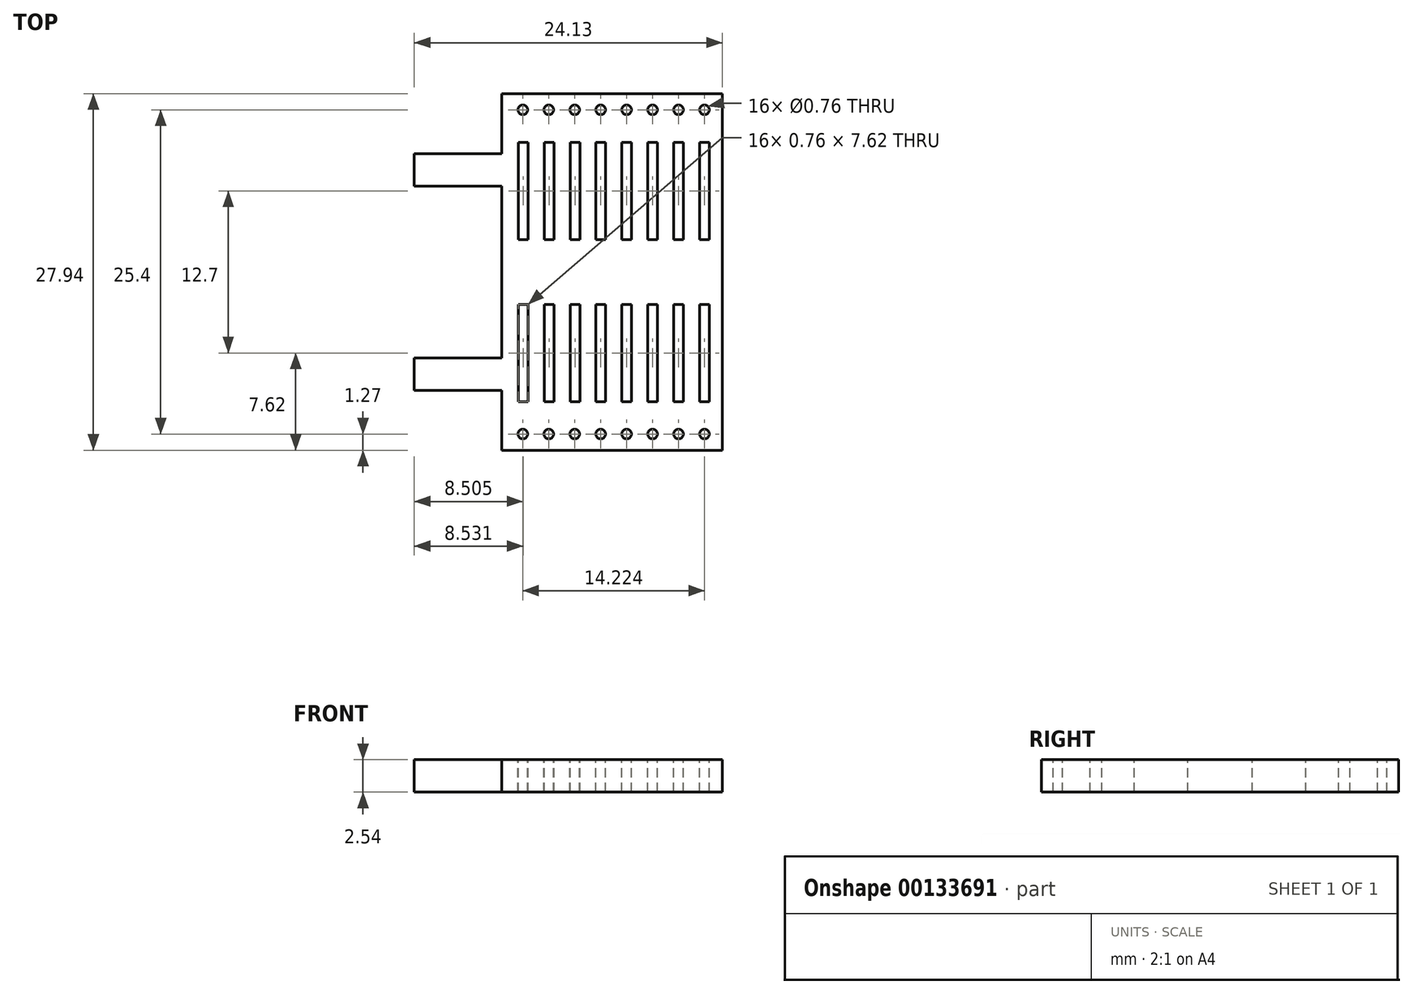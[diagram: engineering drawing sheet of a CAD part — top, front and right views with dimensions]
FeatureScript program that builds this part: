
annotation { "Feature Type Name" : "Feature", "Feature Type Description" : "" }
export const myFeature = defineFeature(function(context is Context, id is Id, definition is map)
    precondition{}
    {
        {
            var Q0;
            Q0=qCreatedBy(makeId("Top.planeOp"),FACE);
            var sketch = newSketch(context, id + "F0", { "sketchPlane" : qUnion([Q0])});
            skLineSegment(sketch, "E0.bottom", {"start": v(8.64, 13.97) * mm, "end": v(-8.64, 13.97) * mm});
            skLineSegment(sketch, "E0.top", {"start": v(8.64, -13.97) * mm, "end": v(-8.64, -13.97) * mm});
            skLineSegment(sketch, "E0.left", {"start": v(8.64, 13.97) * mm, "end": v(8.64, -13.97) * mm});
            skLineSegment(sketch, "E0.right", {"start": v(-8.64, 13.97) * mm, "end": v(-8.64, -13.97) * mm});
            skPoint(sketch, "E0.middle", {"position": v(0, 0) * mm});
            skLineSegment(sketch, "E1.bottom", {"start": v(6.86, 10.16) * mm, "end": v(7.62, 10.16) * mm});
            skLineSegment(sketch, "E1.top", {"start": v(6.86, 2.54) * mm, "end": v(7.62, 2.54) * mm});
            skLineSegment(sketch, "E1.left", {"start": v(6.86, 10.16) * mm, "end": v(6.86, 2.54) * mm});
            skLineSegment(sketch, "E1.right", {"start": v(7.62, 10.16) * mm, "end": v(7.62, 2.54) * mm});
            skCircle(sketch, "E2", {"center": v(7.24, 12.7) * mm, "radius": 0.38 * mm});
            skLineSegment(sketch, "E3.1.0.0", {"start": v(5.6, 10.16) * mm, "end": v(5.6, 2.54) * mm});
            skLineSegment(sketch, "E3.1.0.1", {"start": v(4.83, 10.16) * mm, "end": v(4.83, 2.54) * mm});
            skLineSegment(sketch, "E3.1.0.2", {"start": v(4.83, 10.16) * mm, "end": v(5.6, 10.16) * mm});
            skLineSegment(sketch, "E3.1.0.3", {"start": v(4.83, 2.54) * mm, "end": v(5.6, 2.54) * mm});
            skLineSegment(sketch, "E3.2.0.0", {"start": v(3.56, 10.16) * mm, "end": v(3.56, 2.54) * mm});
            skLineSegment(sketch, "E3.2.0.1", {"start": v(2.8, 10.16) * mm, "end": v(2.8, 2.54) * mm});
            skLineSegment(sketch, "E3.2.0.2", {"start": v(2.8, 10.16) * mm, "end": v(3.56, 10.16) * mm});
            skLineSegment(sketch, "E3.2.0.3", {"start": v(2.8, 2.54) * mm, "end": v(3.56, 2.54) * mm});
            skLineSegment(sketch, "E3.3.0.0", {"start": v(1.54, 10.16) * mm, "end": v(1.54, 2.54) * mm});
            skLineSegment(sketch, "E3.3.0.1", {"start": v(0.77, 10.16) * mm, "end": v(0.77, 2.54) * mm});
            skLineSegment(sketch, "E3.3.0.2", {"start": v(0.77, 10.16) * mm, "end": v(1.54, 10.16) * mm});
            skLineSegment(sketch, "E3.3.0.3", {"start": v(0.77, 2.54) * mm, "end": v(1.54, 2.54) * mm});
            skLineSegment(sketch, "E3.4.0.0", {"start": v(-0.5, 10.16) * mm, "end": v(-0.5, 2.54) * mm});
            skLineSegment(sketch, "E3.4.0.1", {"start": v(-1.26, 10.16) * mm, "end": v(-1.26, 2.54) * mm});
            skLineSegment(sketch, "E3.4.0.2", {"start": v(-1.26, 10.16) * mm, "end": v(-0.5, 10.16) * mm});
            skLineSegment(sketch, "E3.4.0.3", {"start": v(-1.26, 2.54) * mm, "end": v(-0.5, 2.54) * mm});
            skLineSegment(sketch, "E3.5.0.0", {"start": v(-2.52, 10.16) * mm, "end": v(-2.52, 2.54) * mm});
            skLineSegment(sketch, "E3.5.0.1", {"start": v(-3.28, 10.16) * mm, "end": v(-3.28, 2.54) * mm});
            skLineSegment(sketch, "E3.5.0.2", {"start": v(-3.28, 10.16) * mm, "end": v(-2.52, 10.16) * mm});
            skLineSegment(sketch, "E3.5.0.3", {"start": v(-3.28, 2.54) * mm, "end": v(-2.52, 2.54) * mm});
            skLineSegment(sketch, "E3.6.0.0", {"start": v(-4.55, 10.16) * mm, "end": v(-4.55, 2.54) * mm});
            skLineSegment(sketch, "E3.6.0.1", {"start": v(-5.31, 10.16) * mm, "end": v(-5.31, 2.54) * mm});
            skLineSegment(sketch, "E3.6.0.2", {"start": v(-5.31, 10.16) * mm, "end": v(-4.55, 10.16) * mm});
            skLineSegment(sketch, "E3.6.0.3", {"start": v(-5.31, 2.54) * mm, "end": v(-4.55, 2.54) * mm});
            skLineSegment(sketch, "E3.7.0.0", {"start": v(-6.58, 10.16) * mm, "end": v(-6.58, 2.54) * mm});
            skLineSegment(sketch, "E3.7.0.1", {"start": v(-7.34, 10.16) * mm, "end": v(-7.34, 2.54) * mm});
            skLineSegment(sketch, "E3.7.0.2", {"start": v(-7.34, 10.16) * mm, "end": v(-6.58, 10.16) * mm});
            skLineSegment(sketch, "E3.7.0.3", {"start": v(-7.34, 2.54) * mm, "end": v(-6.58, 2.54) * mm});
            skLineSegment(sketch, "E3.direction1", {"start": v(7.62, 2.54) * mm, "end": v(5.6, 2.54) * mm, "construction": true});
            skCircle(sketch, "E4.1.0.0", {"center": v(5.2, 12.7) * mm, "radius": 0.38 * mm});
            skCircle(sketch, "E4.2.0.0", {"center": v(3.17, 12.7) * mm, "radius": 0.38 * mm});
            skCircle(sketch, "E4.3.0.0", {"center": v(1.14, 12.7) * mm, "radius": 0.38 * mm});
            skCircle(sketch, "E4.4.0.0", {"center": v(-0.89, 12.7) * mm, "radius": 0.38 * mm});
            skCircle(sketch, "E4.5.0.0", {"center": v(-2.92, 12.7) * mm, "radius": 0.38 * mm});
            skCircle(sketch, "E4.6.0.0", {"center": v(-4.95, 12.7) * mm, "radius": 0.38 * mm});
            skCircle(sketch, "E4.7.0.0", {"center": v(-6.99, 12.7) * mm, "radius": 0.38 * mm});
            skLineSegment(sketch, "E4.direction1", {"start": v(7.24, 12.7) * mm, "end": v(5.2, 12.7) * mm, "construction": true});
            skLineSegment(sketch, "E5.bottom", {"start": v(-15.5, 9.27) * mm, "end": v(-8.64, 9.27) * mm});
            skLineSegment(sketch, "E5.top", {"start": v(-15.5, 6.73) * mm, "end": v(-8.64, 6.73) * mm});
            skLineSegment(sketch, "E5.left", {"start": v(-15.5, 9.27) * mm, "end": v(-15.5, 6.73) * mm});
            skLineSegment(sketch, "E5.right", {"start": v(-8.64, 9.27) * mm, "end": v(-8.64, 6.73) * mm});
            skLineSegment(sketch, "E6.bottom", {"start": v(-15.5, -6.73) * mm, "end": v(-8.64, -6.73) * mm});
            skLineSegment(sketch, "E6.top", {"start": v(-15.5, -9.27) * mm, "end": v(-8.64, -9.27) * mm});
            skLineSegment(sketch, "E6.left", {"start": v(-15.5, -6.73) * mm, "end": v(-15.5, -9.27) * mm});
            skLineSegment(sketch, "E6.right", {"start": v(-8.64, -6.73) * mm, "end": v(-8.64, -9.27) * mm});
            skLineSegment(sketch, "E7.MirrorCS", {"start": v(6.86, -2.54) * mm, "end": v(7.62, -2.54) * mm});
            skCircle(sketch, "E8.MirrorC", {"center": v(-2.92, -12.7) * mm, "radius": 0.38 * mm});
            skLineSegment(sketch, "E9.MirrorCS", {"start": v(-3.28, -10.16) * mm, "end": v(-3.28, -2.54) * mm});
            skLineSegment(sketch, "E10.MirrorCS", {"start": v(-7.34, -10.16) * mm, "end": v(-7.34, -2.54) * mm});
            skLineSegment(sketch, "E11.MirrorCS", {"start": v(0.77, -10.16) * mm, "end": v(1.54, -10.16) * mm});
            skLineSegment(sketch, "E12.MirrorCS", {"start": v(-7.34, -10.16) * mm, "end": v(-6.58, -10.16) * mm});
            skLineSegment(sketch, "E13.MirrorCS", {"start": v(3.56, -10.16) * mm, "end": v(3.56, -2.54) * mm});
            skLineSegment(sketch, "E14.MirrorCS", {"start": v(2.8, -10.16) * mm, "end": v(2.8, -2.54) * mm});
            skLineSegment(sketch, "E15.MirrorCS", {"start": v(2.8, -10.16) * mm, "end": v(3.56, -10.16) * mm});
            skLineSegment(sketch, "E16.MirrorCS", {"start": v(0.77, -10.16) * mm, "end": v(0.77, -2.54) * mm});
            skCircle(sketch, "E17.MirrorC", {"center": v(5.2, -12.7) * mm, "radius": 0.38 * mm});
            skLineSegment(sketch, "E18.MirrorCS", {"start": v(-5.31, -10.16) * mm, "end": v(-4.55, -10.16) * mm});
            skLineSegment(sketch, "E19.MirrorCS", {"start": v(6.86, -10.16) * mm, "end": v(7.62, -10.16) * mm});
            skLineSegment(sketch, "E20.MirrorCS", {"start": v(-1.26, -10.16) * mm, "end": v(-1.26, -2.54) * mm});
            skLineSegment(sketch, "E21.MirrorCS", {"start": v(-2.52, -10.16) * mm, "end": v(-2.52, -2.54) * mm});
            skCircle(sketch, "E22.MirrorC", {"center": v(-0.89, -12.7) * mm, "radius": 0.38 * mm});
            skLineSegment(sketch, "E23.MirrorCS", {"start": v(-6.58, -10.16) * mm, "end": v(-6.58, -2.54) * mm});
            skLineSegment(sketch, "E24.MirrorCS", {"start": v(1.54, -10.16) * mm, "end": v(1.54, -2.54) * mm});
            skLineSegment(sketch, "E25.MirrorCS", {"start": v(-5.31, -10.16) * mm, "end": v(-5.31, -2.54) * mm});
            skLineSegment(sketch, "E26.MirrorCS", {"start": v(7.62, -2.54) * mm, "end": v(5.6, -2.54) * mm, "construction": true});
            skLineSegment(sketch, "E27.MirrorCS", {"start": v(-0.5, -10.16) * mm, "end": v(-0.5, -2.54) * mm});
            skLineSegment(sketch, "E28.MirrorCS", {"start": v(-1.26, -2.54) * mm, "end": v(-0.5, -2.54) * mm});
            skLineSegment(sketch, "E29.MirrorCS", {"start": v(-3.28, -2.54) * mm, "end": v(-2.52, -2.54) * mm});
            skCircle(sketch, "E30.MirrorC", {"center": v(1.14, -12.7) * mm, "radius": 0.38 * mm});
            skCircle(sketch, "E31.MirrorC", {"center": v(-6.99, -12.7) * mm, "radius": 0.38 * mm});
            skLineSegment(sketch, "E32.MirrorCS", {"start": v(-5.31, -2.54) * mm, "end": v(-4.55, -2.54) * mm});
            skLineSegment(sketch, "E33.MirrorCS", {"start": v(2.8, -2.54) * mm, "end": v(3.56, -2.54) * mm});
            skLineSegment(sketch, "E34.MirrorCS", {"start": v(-7.34, -2.54) * mm, "end": v(-6.58, -2.54) * mm});
            skLineSegment(sketch, "E35.MirrorCS", {"start": v(-4.55, -10.16) * mm, "end": v(-4.55, -2.54) * mm});
            skLineSegment(sketch, "E36.MirrorCS", {"start": v(7.24, -12.7) * mm, "end": v(5.2, -12.7) * mm, "construction": true});
            skLineSegment(sketch, "E37.MirrorCS", {"start": v(0.77, -2.54) * mm, "end": v(1.54, -2.54) * mm});
            skLineSegment(sketch, "E38.MirrorCS", {"start": v(-1.26, -10.16) * mm, "end": v(-0.5, -10.16) * mm});
            skCircle(sketch, "E39.MirrorC", {"center": v(3.17, -12.7) * mm, "radius": 0.38 * mm});
            skLineSegment(sketch, "E40.MirrorCS", {"start": v(4.83, -2.54) * mm, "end": v(5.6, -2.54) * mm});
            skLineSegment(sketch, "E41.MirrorCS", {"start": v(4.83, -10.16) * mm, "end": v(5.6, -10.16) * mm});
            skLineSegment(sketch, "E42.MirrorCS", {"start": v(-3.28, -10.16) * mm, "end": v(-2.52, -10.16) * mm});
            skLineSegment(sketch, "E43.MirrorCS", {"start": v(4.83, -10.16) * mm, "end": v(4.83, -2.54) * mm});
            skLineSegment(sketch, "E44.MirrorCS", {"start": v(5.6, -10.16) * mm, "end": v(5.6, -2.54) * mm});
            skCircle(sketch, "E45.MirrorC", {"center": v(7.24, -12.7) * mm, "radius": 0.38 * mm});
            skLineSegment(sketch, "E46.MirrorCS", {"start": v(7.62, -10.16) * mm, "end": v(7.62, -2.54) * mm});
            skLineSegment(sketch, "E47.MirrorCS", {"start": v(6.86, -10.16) * mm, "end": v(6.86, -2.54) * mm});
            skCircle(sketch, "E48.MirrorC", {"center": v(-4.95, -12.7) * mm, "radius": 0.38 * mm});
            skSolve(sketch);
        }
        {
            var Q0;
            Q0=makeQuery(id+"F0.imprint","IMPRINT",FACE,{"disambiguationData":[TD([[makeQuery(id+"F0.imprint","IMPRINT",EDGE,{"derivedFrom":sQuery(id+"F0.wireOp",EDGE,"E5.bottom")}),-1.0]])]});
            var Q1;
            Q1=makeQuery(id+"F0.imprint","IMPRINT",FACE,{"disambiguationData":[TD([[makeQuery(id+"F0.imprint","IMPRINT",EDGE,{"derivedFrom":sQuery(id+"F0.wireOp",EDGE,"E6.bottom")}),-1.0]])]});
            var Q2;
            {var subQ3=sQuery(id+"F0.wireOp",EDGE,"E0.bottom");Q2=makeQuery(id+"F0.imprint","IMPRINT",FACE,{"disambiguationData":[TD([[makeQuery(id+"F0.imprint","IMPRINT",EDGE,{"derivedFrom":subQ3}),1.0]])]});}
            extrude(context, id + "F1", {"entities" : qUnion([Q0, Q1, Q2]), "oppositeDirection" : true, "depth" : 2.54 * mm});
        }
    });
